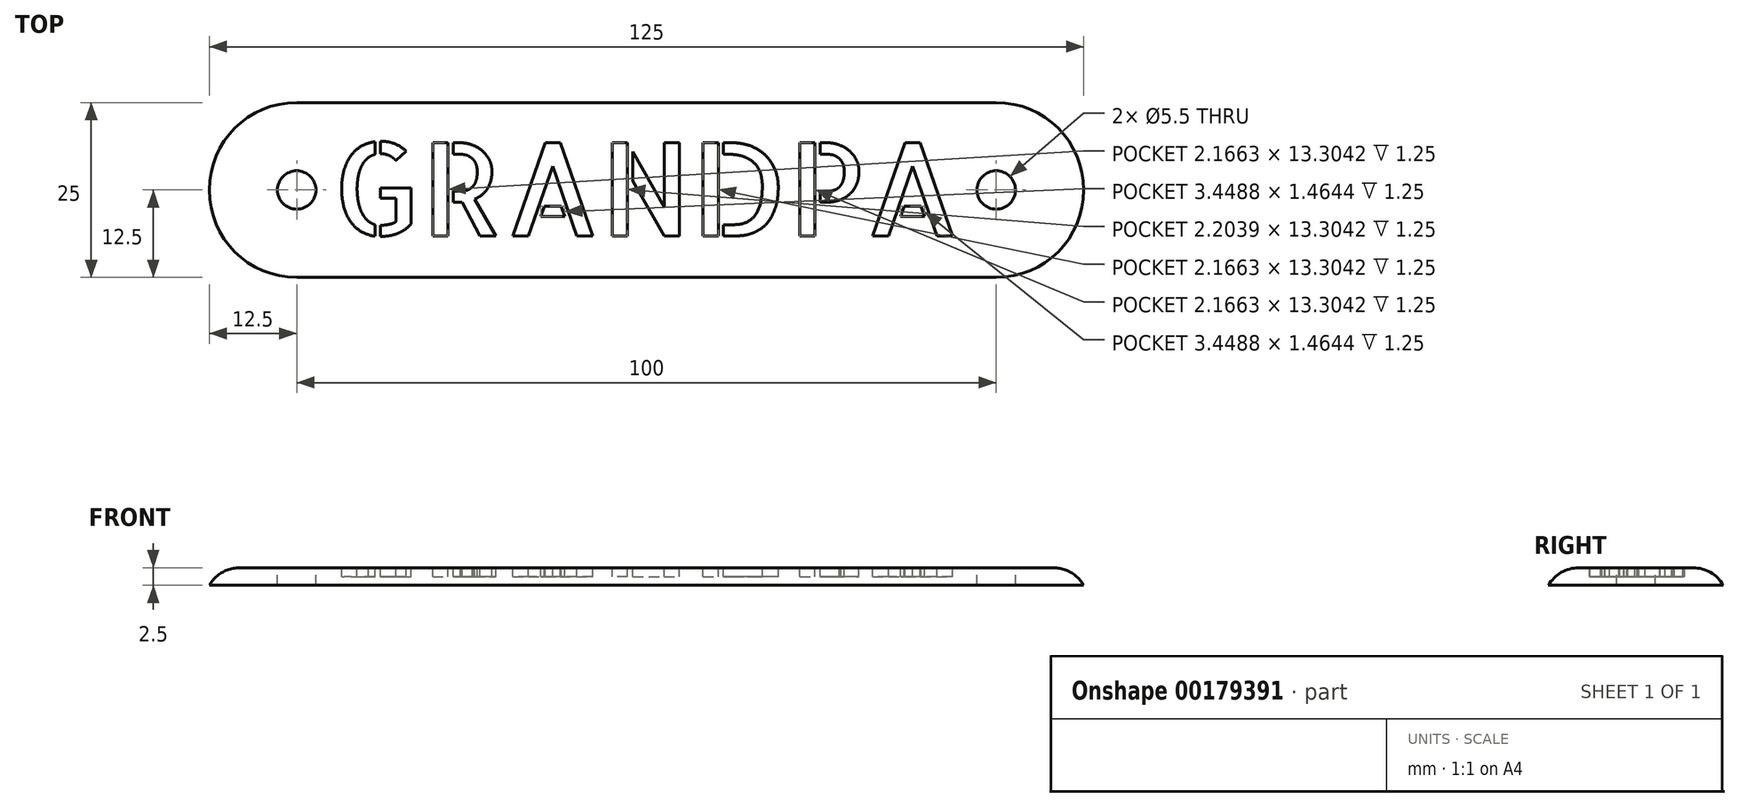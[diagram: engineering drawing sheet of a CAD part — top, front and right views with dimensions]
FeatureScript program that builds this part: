
annotation { "Feature Type Name" : "Feature", "Feature Type Description" : "" }
export const myFeature = defineFeature(function(context is Context, id is Id, definition is map)
    precondition{}
    {
        {
            var Q0;
            Q0=qCreatedBy(makeId("Top.planeOp"),FACE);
            var sketch = newSketch(context, id + "F0", { "sketchPlane" : qUnion([Q0])});
            skLineSegment(sketch, "E0.bottom", {"start": v(-50, 12.5) * mm, "end": v(50, 12.5) * mm});
            skLineSegment(sketch, "E0.top", {"start": v(-50, -12.5) * mm, "end": v(50, -12.5) * mm});
            skLineSegment(sketch, "E0.left", {"start": v(-50, 12.5) * mm, "end": v(-50, -12.5) * mm});
            skLineSegment(sketch, "E0.right", {"start": v(50, 12.5) * mm, "end": v(50, -12.5) * mm});
            skPoint(sketch, "E0.middle", {"position": v(0, 0) * mm});
            skArc(sketch, "E1", {"start": v(-50, 12.5) * mm, "mid": v(-62.5, 0) * mm, "end": v(-50, -12.5) * mm});
            skArc(sketch, "E2", {"start": v(50, -12.5) * mm, "mid": v(62.5, 0) * mm, "end": v(50, 12.5) * mm});
            skSolve(sketch);
        }
        {
            var Q0;
            Q0=makeQuery(id+"F0.imprint","IMPRINT",FACE,{"disambiguationData":[TD([[makeQuery(id+"F0.imprint","IMPRINT",EDGE,{"derivedFrom":sQuery(id+"F0.wireOp",EDGE,"E0.bottom")}),-1.0]])]});
            var Q1;
            Q1=makeQuery(id+"F0.imprint","IMPRINT",FACE,{"disambiguationData":[TD([[makeQuery(id+"F0.imprint","IMPRINT",EDGE,{"derivedFrom":sQuery(id+"F0.wireOp",EDGE,"E0.left")}),-1.0]])]});
            var Q2;
            Q2=makeQuery(id+"F0.imprint","IMPRINT",FACE,{"disambiguationData":[TD([[makeQuery(id+"F0.imprint","IMPRINT",EDGE,{"derivedFrom":sQuery(id+"F0.wireOp",EDGE,"E0.right")}),1.0]])]});
            extrude(context, id + "F1", {"entities" : qUnion([Q0, Q1, Q2]), "depth" : 2.5 * mm});
        }
        {
            var Q0;
            Q0=makeQuery(id+"F1.opExtrude","CAP_FACE",FACE,{"disambiguationData":[OSD([sQuery(id+"F0.wireOp",EDGE,"E0.bottom"),sQuery(id+"F0.wireOp",EDGE,"E0.top"),sQuery(id+"F0.wireOp",EDGE,"E0.left"),sQuery(id+"F0.wireOp",EDGE,"E0.right")])],"isStart":false});
            var sketch = newSketch(context, id + "F2", { "sketchPlane" : qUnion([Q0])});
            skText(sketch, "E3", { "text": "GRANDPA", "fontName": "AllertaStencil-Regular.ttf"});
            const initialGuessF2  = {"E3": [-0.045, -0.00655, 1, 0, 0.01331]};
            skSetInitialGuess(sketch, initialGuessF2);
            skSolve(sketch);
        }
        {
            var Q0;
            Q0 = qSketchRegion(id + "F2", true);
            extrude(context, id + "F3", {"entities" : qUnion([Q0]), "operationType" : NewBodyOperationType.REMOVE, "oppositeDirection" : true, "depth" : 1.25 * mm});
        }
        {
            var Q0;
            Q0=makeQuery(id+"F1.opExtrude","CAP_FACE",FACE,{"disambiguationData":[OSD([sQuery(id+"F0.wireOp",EDGE,"E0.bottom"),sQuery(id+"F0.wireOp",EDGE,"E0.top"),sQuery(id+"F0.wireOp",EDGE,"E1"),sQuery(id+"F0.wireOp",EDGE,"E2")])],"isStart":false});
            var sketch = newSketch(context, id + "F4", { "sketchPlane" : qUnion([Q0])});
            skLineSegment(sketch, "E4", {"start": v(-50, 12.5) * mm, "end": v(-50, -12.5) * mm, "construction": true});
            skPoint(sketch, "E5", {"position": v(-50, 0) * mm});
            skLineSegment(sketch, "E6", {"start": v(50, -12.5) * mm, "end": v(50, 12.5) * mm, "construction": true});
            skPoint(sketch, "E7", {"position": v(50, 0) * mm});
            skSolve(sketch);
        }
        {
            var Q0;
            Q0=sQuery(id+"F4.wireOp",VERTEX,"E5");
            var Q1;
            Q1=sQuery(id+"F4.wireOp",VERTEX,"E7");
            var Q2;
            Q2=makeQuery(id+"F1.opExtrude","SWEPT_BODY",BODY,{"disambiguationData":[OSD([sQuery(id+"F0.wireOp",EDGE,"E0.bottom"),sQuery(id+"F0.wireOp",EDGE,"E0.top"),sQuery(id+"F0.wireOp",EDGE,"E1"),sQuery(id+"F0.wireOp",EDGE,"E2")])]});
            hole(context, id + "F5", {"style" : HoleStyle.SIMPLE, "endStyle" : HoleEndStyle.THROUGH, "holeDiameter" : 5.5 * mm, "locations" : qUnion([Q0, Q1]), "scope" : qUnion([Q2]), "isTappedThrough" : true});
        }
        {
            var Q0;
            Q0=makeQuery(id+"F1.opExtrude","CAP_EDGE",EDGE,{"disambiguationData":[OSD([sQuery(id+"F0.wireOp",EDGE,"E0.top")])],"isStart":false});
            fillet(context, id + "F6", {"entities" : qUnion([Q0]), "radius" : 5 * mm, "tangentPropagation" : true, "allowEdgeOverflow" : false});
        }
    });
